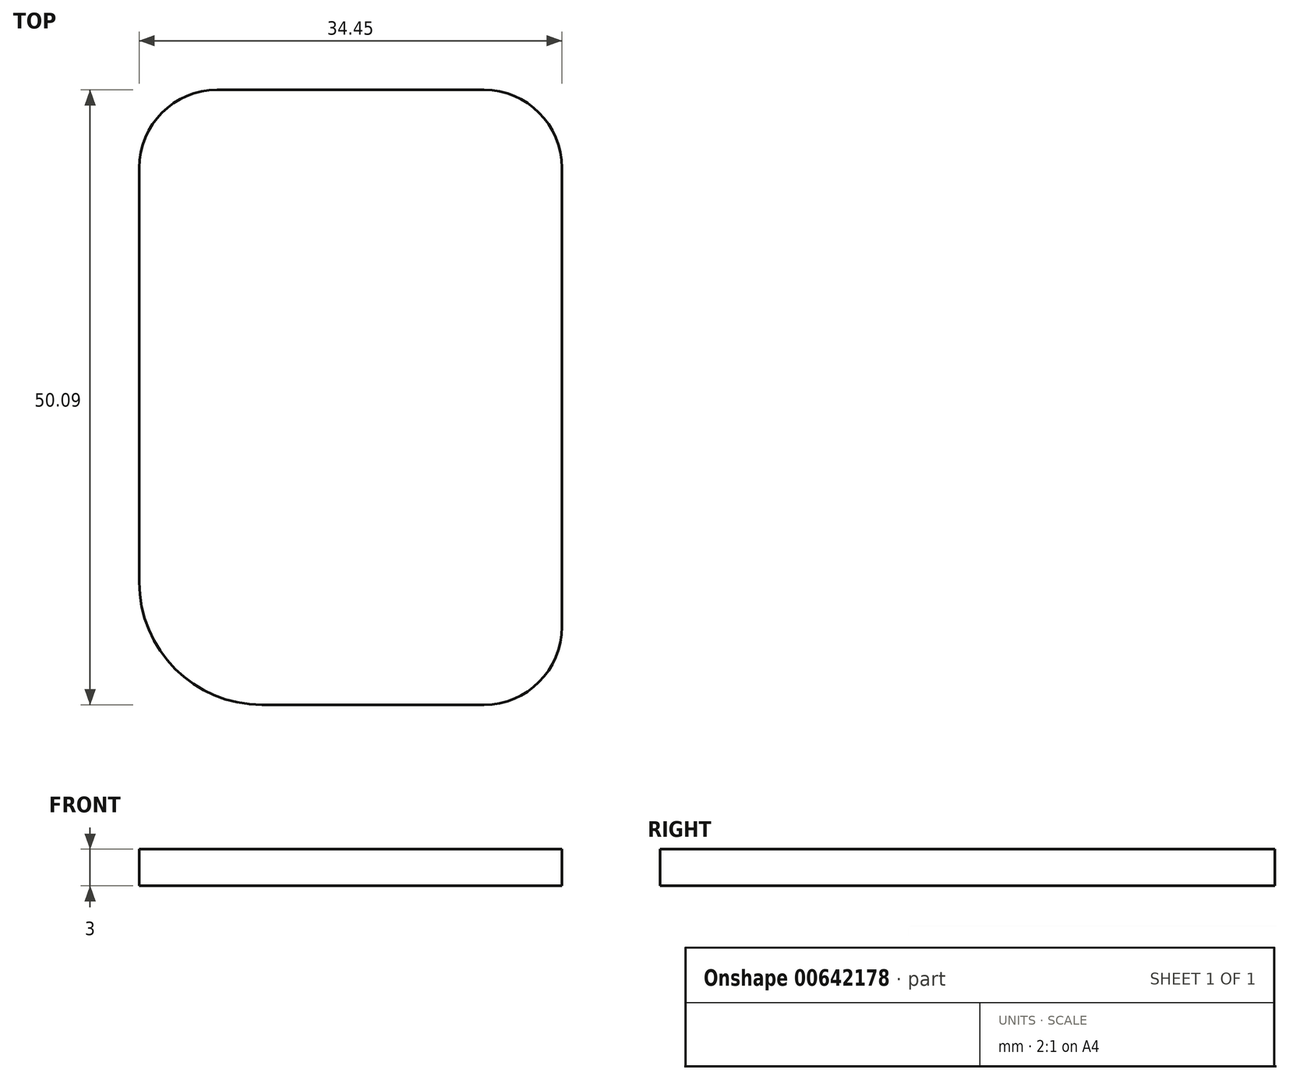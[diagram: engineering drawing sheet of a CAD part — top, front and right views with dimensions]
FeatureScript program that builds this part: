
annotation { "Feature Type Name" : "Feature", "Feature Type Description" : "" }
export const myFeature = defineFeature(function(context is Context, id is Id, definition is map)
    precondition{}
    {
        {
            var Q0;
            Q0=qCreatedBy(makeId("Top.planeOp"),FACE);
            var sketch = newSketch(context, id + "F0", { "sketchPlane" : qUnion([Q0])});
            skLineSegment(sketch, "E0.bottom", {"start": v(6.35, 0) * mm, "end": v(28.1, 0) * mm});
            skLineSegment(sketch, "E0.top", {"start": v(10, -50.1) * mm, "end": v(28.1, -50.1) * mm});
            skLineSegment(sketch, "E0.left", {"start": v(0, -6.35) * mm, "end": v(0, -40.1) * mm});
            skLineSegment(sketch, "E0.right", {"start": v(34.45, -6.35) * mm, "end": v(34.45, -43.74) * mm});
            skPoint(sketch, "E1.visualSharp", {"position": v(0, 0) * mm});
            skArc(sketch, "E1.filletArc", {"start": v(6.35, 0) * mm, "mid": v(1.86, -1.86) * mm, "end": v(0, -6.35) * mm});
            skPoint(sketch, "E2.visualSharp", {"position": v(34.45, 0) * mm});
            skArc(sketch, "E2.filletArc", {"start": v(34.45, -6.35) * mm, "mid": v(32.6, -1.86) * mm, "end": v(28.1, 0) * mm});
            skPoint(sketch, "E3.visualSharp", {"position": v(34.45, -50.1) * mm});
            skArc(sketch, "E3.filletArc", {"start": v(28.1, -50.1) * mm, "mid": v(32.6, -48.23) * mm, "end": v(34.45, -43.74) * mm});
            skPoint(sketch, "E4.visualSharp", {"position": v(0, -50.1) * mm});
            skArc(sketch, "E4.filletArc", {"start": v(0, -40.1) * mm, "mid": v(2.93, -47.16) * mm, "end": v(10, -50.1) * mm});
            skSolve(sketch);
        }
        {
            var Q0;
            Q0=makeQuery(id+"F0.imprint","IMPRINT",FACE,{"disambiguationData":[TD([[makeQuery(id+"F0.imprint","IMPRINT",EDGE,{"derivedFrom":sQuery(id+"F0.wireOp",EDGE,"E0.bottom")}),-1.0]])]});
            extrude(context, id + "F1", {"entities" : qUnion([Q0]), "depth" : 3 * mm, "offsetDistance" : 25.4 * mm});
        }
    });
